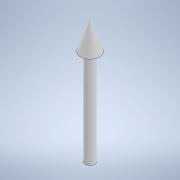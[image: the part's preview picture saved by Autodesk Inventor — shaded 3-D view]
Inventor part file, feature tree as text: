
AUTODESK INVENTOR PART (.ipt)
format: ipt  version: 2021 (Build 250183000, 183)  size: 102,400 bytes
history: native  units: mm
features: extrude x2, sketch x2, other x1, chamfer x1
ambient origin geometry x8: Origin, YZ Plane, XZ Plane, XY Plane, X Axis, Y Axis, Z Axis, Center Point
bodies: Body1 (feature_tree)
feature tree (6):
  other  "實體1"
  extrude  "擠出1"  Depth=1.0mm
  extrude  "擠出2"  Depth=10.0mm TaperAngle=0.0deg
  chamfer  "倒角1"  Distance=2.0mm
  sketch  "草圖1"
  sketch  "草圖2"
